# Revit family: Toilet-Floor_Mount-KOHLER-ESCALE-K-3588T_1
name_source: partatom
category: Plumbing Fixtures
units: mm (PartAtom-declared; Revit-internal decimal feet)

## family parameters
Cut with Voids When Loaded = No
Host = Face
OmniClass Number = 23.31.19.00
OmniClass Title = Toilets
Part Type = Normal
Room Calculation Point = No
Round Connector Dimension = Use Diameter
Shared = No

## types (2) — shared parameters
ADA Compliant = No
Assembly Code = D2010100
CW Connection = Yes
Cold Water Inlet = Cold Water Inlet
Date Modified = 08/18/2023
Default Elevation = 0"
Finish = Kohler-Vitreous_China-0-White
Flow Rate = 0 GPM
Flush Rate- GPF = 0
Flush Rate- LPF = 0
HW Connection = No
Height = 33 5/8"
Hot Water Inlet = Hot Water Inlet
Length = 26 15/16"
Manufacturer = Kohler Co.
Master Format 2014 = 22 42 13.13
Master Format 2014 Name = Residential Water Closets
Material = Vitreous China
Pressure = 0.00 psi
Product Name = ESCALE
Rough-In for P-Trap = 6 3/8"
Rough-In for S-Trap = 12"
Seat Included = Yes
URL = http://www.kohler.com.cn
Vent Connection = No
Waste Connection = Yes
Waste Water Outlet = Waste Water Outlet
WaterSense Certified = No
Width = 15 11/16"

## per-type parameters (varying)
| type | Angle 1 | Description | Distance | Distance 1 | Distance 2 | H | Model | Product Documentation Link | Type |
| S-Trap, 0-White | 90.00° | SKIRTE TWO PIECE DUAL FLUSH 3/6L WASH | 6 3/8" | 11" | 1 15/16" | Yes | K-3588T-H-0 | https://files.kohler.com.cn | 1 |
| P-Trap, 0-White | 0.00° | Two-piece dual flush toilet, 305mm | 11" | 0" | 0" | No | K-3588T-S2-0 |  | 2 |

## geometry (parser evidence)
native form markers: Sweep x6
no freeform markers — native parametric forms only
